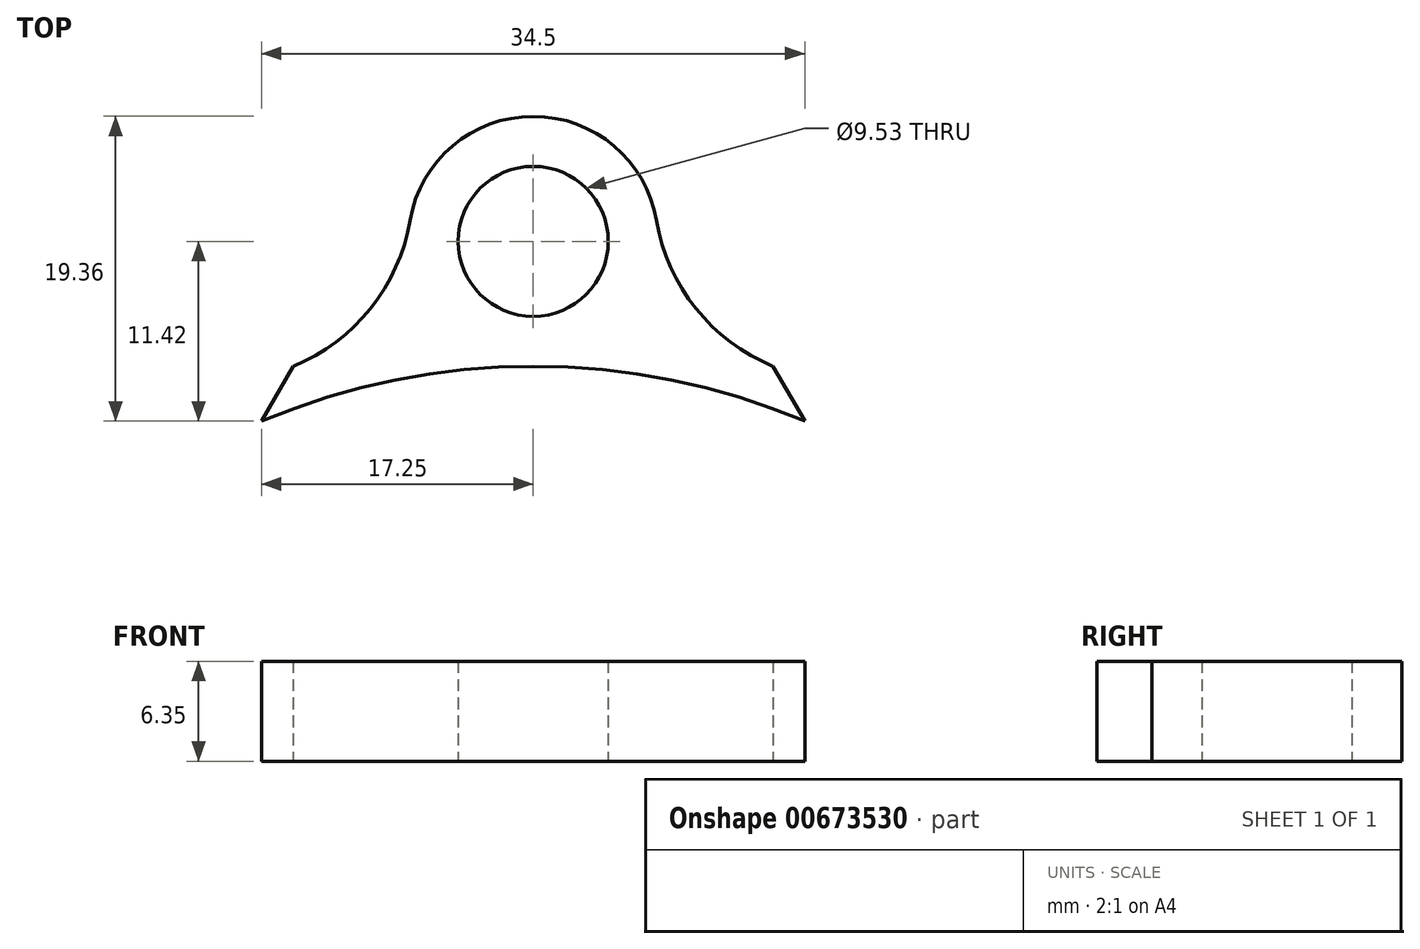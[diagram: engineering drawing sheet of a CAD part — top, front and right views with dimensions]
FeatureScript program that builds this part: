
annotation { "Feature Type Name" : "Feature", "Feature Type Description" : "" }
export const myFeature = defineFeature(function(context is Context, id is Id, definition is map)
    precondition{}
    {
        {
            var Q0;
            Q0=qCreatedBy(makeId("Top.planeOp"),FACE);
            var sketch = newSketch(context, id + "F0", { "sketchPlane" : qUnion([Q0])});
            skCircle(sketch, "E0", {"center": v(0, 0) * mm, "radius": 4.76 * mm});
            skArc(sketch, "E1", {"start": v(17.25, -11.42) * mm, "mid": v(0, -7.94) * mm, "end": v(-17.25, -11.42) * mm});
            skLineSegment(sketch, "E2", {"start": v(-17.25, -11.42) * mm, "end": v(-15.24, -7.94) * mm});
            skArc(sketch, "E3", {"start": v(-15.24, -7.94) * mm, "mid": v(-10.33, -4.26) * mm, "end": v(-7.83, 1.33) * mm});
            skArc(sketch, "E4", {"start": v(7.83, 1.33) * mm, "mid": v(0, 7.94) * mm, "end": v(-7.83, 1.33) * mm});
            skArc(sketch, "E5", {"start": v(7.83, 1.33) * mm, "mid": v(10.33, -4.26) * mm, "end": v(15.24, -7.94) * mm});
            skLineSegment(sketch, "E6", {"start": v(17.25, -11.42) * mm, "end": v(15.24, -7.94) * mm});
            skLineSegment(sketch, "E7", {"start": v(-15.24, -7.94) * mm, "end": v(-20.76, -7.94) * mm, "construction": true});
            skLineSegment(sketch, "E8", {"start": v(0, -7.94) * mm, "end": v(0, -4.76) * mm, "construction": true});
            skLineSegment(sketch, "E9", {"start": v(-15.24, -7.94) * mm, "end": v(-14.42, -10.34) * mm, "construction": true});
            skSolve(sketch);
        }
        {
            var Q0;
            Q0 = qSketchRegion(id + "F0", true);
            extrude(context, id + "F1", {"entities" : qUnion([Q0]), "depth" : 6.35 * mm, "offsetDistance" : 25.4 * mm});
        }
    });
